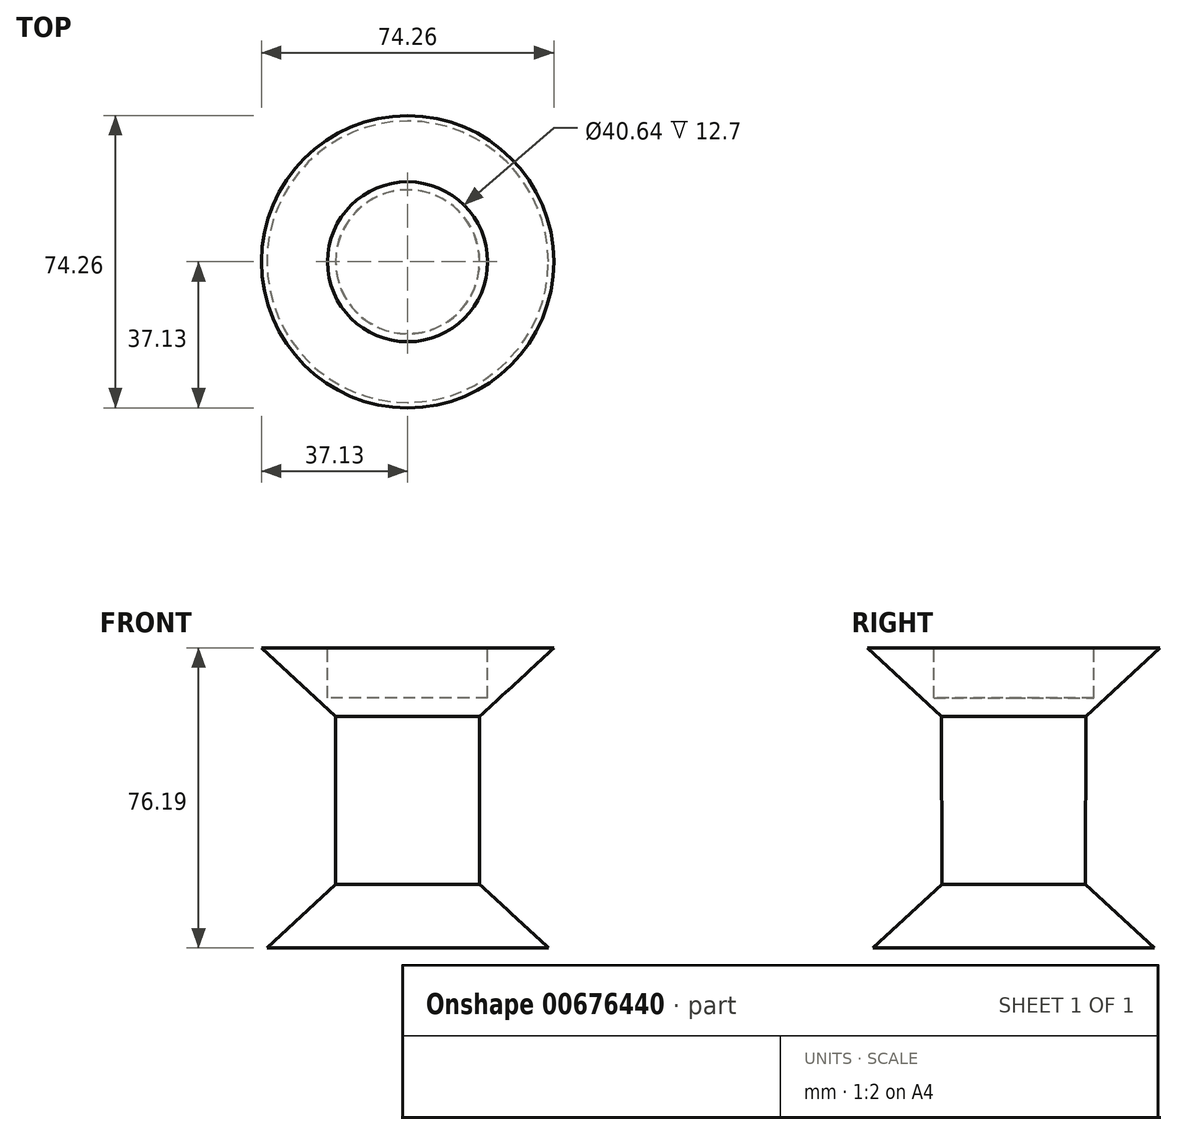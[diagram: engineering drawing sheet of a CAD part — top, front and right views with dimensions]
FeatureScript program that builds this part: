
annotation { "Feature Type Name" : "Feature", "Feature Type Description" : "" }
export const myFeature = defineFeature(function(context is Context, id is Id, definition is map)
    precondition{}
    {
        {
            var Q0;
            Q0=qCreatedBy(makeId("Front.planeOp"),FACE);
            var sketch = newSketch(context, id + "F0", { "sketchPlane" : qUnion([Q0])});
            skLineSegment(sketch, "E0.MirrorCS", {"start": v(37.13, 76.19) * mm, "end": v(18.31, 58.78) * mm});
            skLineSegment(sketch, "E1.MirrorCS", {"start": v(18.31, 58.78) * mm, "end": v(18.25, 16.18) * mm});
            skLineSegment(sketch, "E2.MirrorCS", {"start": v(18.25, 16.18) * mm, "end": v(35.74, 0) * mm});
            skLineSegment(sketch, "E3", {"start": v(0, 0) * mm, "end": v(35.74, 0) * mm});
            skLineSegment(sketch, "E4", {"start": v(20.32, 76.19) * mm, "end": v(37.13, 76.19) * mm});
            skLineSegment(sketch, "E5", {"start": v(0, 63.49) * mm, "end": v(20.32, 63.49) * mm});
            skLineSegment(sketch, "E6", {"start": v(20.32, 76.19) * mm, "end": v(20.32, 63.49) * mm});
            skLineSegment(sketch, "E7", {"start": v(0, 63.49) * mm, "end": v(0, 0) * mm});
            skSolve(sketch);
        }
        {
            var Q0;
            Q0=makeQuery(id+"F0.imprint","IMPRINT",FACE,{"disambiguationData":[TD([[makeQuery(id+"F0.imprint","IMPRINT",EDGE,{"derivedFrom":sQuery(id+"F0.wireOp",EDGE,"E0.MirrorCS")}),-1.0]])]});
            var Q1;
            Q1=sQuery(id+"F0.wireOp",EDGE,"E7");
            revolve(context, id + "F1", {"entities" : qUnion([Q0]), "axis" : qUnion([Q1]), "revolveType" : RevolveType.FULL});
        }
    });
